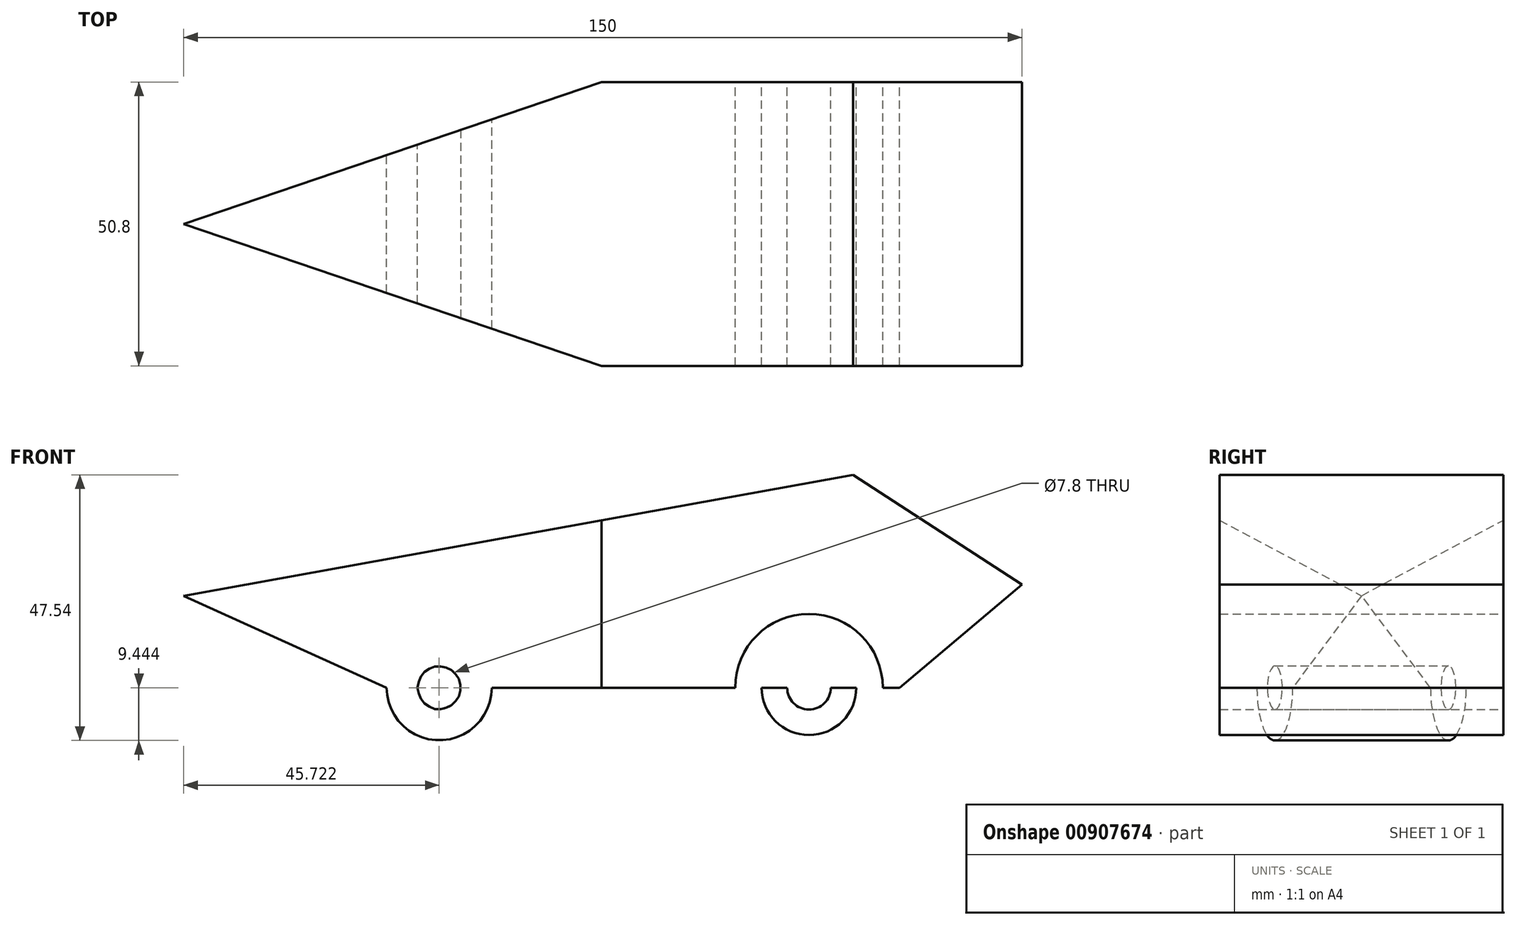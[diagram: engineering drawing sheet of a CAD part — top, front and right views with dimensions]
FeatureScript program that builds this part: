
annotation { "Feature Type Name" : "Feature", "Feature Type Description" : "" }
export const myFeature = defineFeature(function(context is Context, id is Id, definition is map)
    precondition{}
    {
        {
            var Q0;
            Q0=qCreatedBy(makeId("Front.planeOp"),FACE);
            var sketch = newSketch(context, id + "F0", { "sketchPlane" : qUnion([Q0])});
            skLineSegment(sketch, "E0", {"start": v(-74.79, -2) * mm, "end": v(44.98, 19.63) * mm});
            skLineSegment(sketch, "E1", {"start": v(44.98, 19.63) * mm, "end": v(75.21, 0) * mm});
            skLineSegment(sketch, "E2", {"start": v(75.21, 0) * mm, "end": v(53.35, -18.47) * mm});
            skLineSegment(sketch, "E3", {"start": v(53.35, -18.47) * mm, "end": v(-38.5, -18.47) * mm});
            skLineSegment(sketch, "E4", {"start": v(-38.5, -18.47) * mm, "end": v(-74.79, -2) * mm});
            skCircle(sketch, "E5", {"center": v(-29.07, -18.47) * mm, "radius": 13.2 * mm});
            skCircle(sketch, "E6", {"center": v(37.11, -18.47) * mm, "radius": 13.2 * mm});
            skCircle(sketch, "E7", {"center": v(37.11, -18.47) * mm, "radius": 3.9 * mm});
            skCircle(sketch, "E8", {"center": v(-29.07, -18.47) * mm, "radius": 3.9 * mm});
            skArc(sketch, "E9", {"start": v(-38.5, -18.47) * mm, "mid": v(-29.07, -27.9) * mm, "end": v(-19.63, -18.47) * mm});
            skArc(sketch, "E10", {"start": v(28.64, -18.47) * mm, "mid": v(37.11, -26.94) * mm, "end": v(45.59, -18.47) * mm});
            skSolve(sketch);
        }
        {
            var Q0;
            Q0=makeQuery(id+"F0.imprint","IMPRINT",FACE,{"disambiguationData":[TD([[makeQuery(id+"F0.imprint","IMPRINT",EDGE,{"derivedFrom":sQuery(id+"F0.wireOp",EDGE,"E0")}),-1.0]])]});
            var Q1;
            {var subQ0=sQuery(id+"F0.wireOp",EDGE,"E6");var subQ1=sQuery(id+"F0.wireOp",EDGE,"E3");var subQ2=makeQuery(id+"F0.imprint","INTERSECT",VERTEX,{"disambiguationData":[OD(0.0)],"derivedFrom":[subQ1,subQ0]});Q1=makeQuery(id+"F0.imprint","IMPRINT",FACE,{"disambiguationData":[TD([[makeQuery(id+"F0.imprint","IMPRINT",EDGE,{"disambiguationData":[TD([[subQ2,-1.0]])],"derivedFrom":subQ1}),-1.0]])]});}
            var Q2;
            {var subQ1=sQuery(id+"F0.wireOp",EDGE,"E3");var subQ3=sQuery(id+"F0.wireOp",EDGE,"E5");var subQ7=makeQuery(id+"F0.imprint","INTERSECT",VERTEX,{"derivedFrom":[subQ1,subQ3]});Q2=makeQuery(id+"F0.imprint","IMPRINT",FACE,{"disambiguationData":[TD([[makeQuery(id+"F0.imprint","IMPRINT",EDGE,{"disambiguationData":[TD([[subQ7,-1.0]])],"derivedFrom":subQ1}),-1.0]])]});}
            var Q3;
            {var subQ0=sQuery(id+"F0.wireOp",EDGE,"E9");Q3=makeQuery(id+"F0.imprint","IMPRINT",FACE,{"disambiguationData":[TD([[makeQuery(id+"F0.imprint","IMPRINT",EDGE,{"derivedFrom":subQ0}),1.0]])]});}
            var Q4;
            {var subQ0=sQuery(id+"F0.wireOp",EDGE,"E10");Q4=makeQuery(id+"F0.imprint","IMPRINT",FACE,{"disambiguationData":[TD([[makeQuery(id+"F0.imprint","IMPRINT",EDGE,{"derivedFrom":subQ0}),1.0]])]});}
            extrude(context, id + "F1", {"entities" : qUnion([Q0, Q1, Q2, Q3, Q4]), "endBound" : BoundingType.SYMMETRIC, "depth" : 50.8 * mm, "offsetDistance" : 25.4 * mm});
        }
        {
            var Q0;
            {var subQ0=sQuery(id+"F0.wireOp",EDGE,"E4");var subQ1=sQuery(id+"F0.wireOp",EDGE,"E3");var subQ2=makeQuery(id+"F0.imprint","INTERSECT",VERTEX,{"derivedFrom":[subQ1,subQ0]});Q0=makeQuery(id+"F0.imprint","IMPRINT",FACE,{"disambiguationData":[TD([[makeQuery(id+"F0.imprint","IMPRINT",EDGE,{"disambiguationData":[TD([[subQ2,1.0]])],"derivedFrom":subQ1}),-1.0]])]});}
            var Q1;
            {var subQ0=sQuery(id+"F0.wireOp",EDGE,"E6");var subQ1=sQuery(id+"F0.wireOp",EDGE,"E3");var subQ2=makeQuery(id+"F0.imprint","INTERSECT",VERTEX,{"disambiguationData":[OD(0.0)],"derivedFrom":[subQ1,subQ0]});Q1=makeQuery(id+"F0.imprint","IMPRINT",FACE,{"disambiguationData":[TD([[makeQuery(id+"F0.imprint","IMPRINT",EDGE,{"disambiguationData":[TD([[subQ2,-1.0]])],"derivedFrom":subQ1}),-1.0]])]});}
            extrude(context, id + "F2", {"entities" : qUnion([Q0, Q1]), "operationType" : NewBodyOperationType.ADD, "endBound" : BoundingType.SYMMETRIC, "depth" : 25.4 * mm, "offsetDistance" : 25.4 * mm});
        }
        {
            var Q0;
            Q0=qCreatedBy(makeId("Top.planeOp"),FACE);
            var sketch = newSketch(context, id + "F3", { "sketchPlane" : qUnion([Q0])});
            skLineSegment(sketch, "E11", {"start": v(-74.79, 0) * mm, "end": v(0, 25.4) * mm});
            skLineSegment(sketch, "E12", {"start": v(0, 25.4) * mm, "end": v(0, -25.4) * mm});
            skLineSegment(sketch, "E13", {"start": v(0, -25.4) * mm, "end": v(-74.79, 0) * mm});
            skLineSegment(sketch, "E14", {"start": v(0, 25.4) * mm, "end": v(0, 56.22) * mm});
            skLineSegment(sketch, "E15", {"start": v(0, 56.22) * mm, "end": v(-99.16, 56.22) * mm});
            skLineSegment(sketch, "E16", {"start": v(-99.16, 56.22) * mm, "end": v(-99.16, -55.5) * mm});
            skLineSegment(sketch, "E17", {"start": v(-99.16, -55.5) * mm, "end": v(0, -55.5) * mm});
            skLineSegment(sketch, "E18", {"start": v(0, -55.5) * mm, "end": v(0, -25.4) * mm});
            skSolve(sketch);
        }
        {
            var Q0;
            Q0=makeQuery(id+"F3.imprint","IMPRINT",FACE,{"disambiguationData":[TD([[makeQuery(id+"F3.imprint","IMPRINT",EDGE,{"derivedFrom":sQuery(id+"F3.wireOp",EDGE,"E11")}),1.0]])]});
            extrude(context, id + "F4", {"entities" : qUnion([Q0]), "operationType" : NewBodyOperationType.REMOVE, "endBound" : BoundingType.SYMMETRIC, "oppositeDirection" : true, "depth" : 203.2 * mm, "offsetDistance" : 25.4 * mm});
        }
    });
